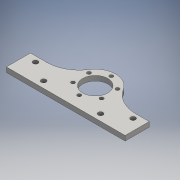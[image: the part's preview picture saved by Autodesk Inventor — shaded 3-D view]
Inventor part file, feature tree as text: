
AUTODESK INVENTOR PART (.ipt)
format: ipt  version: 2016 (Build 200138000, 138)  size: 146,432 bytes
history: native  units: mm
features: reference x13, extrude x4, sketch x4, fillet x1
ambient origin geometry x8: Origin, YZ Plane, XZ Plane, XY Plane, X Axis, Y Axis, Z Axis, Center Point
bodies: Solid1 (feature_tree)
feature tree (22):
  extrude  "Extrusion1"  Depth=6.0mm TaperAngle=0.0deg
  extrude  "Extrusion2"  Depth=6.0mm
  extrude  "Extrusion3"  Depth=60.0mm
  extrude  "Extrusion4"  Depth=40.0mm
  fillet  "Fillet2"  Radius=35.0mm
  sketch  "Sketch1"  dims[d0=34.0mm d1=6.0mm d2=0.0mm]
  reference  "Reference1"
  reference  "Reference2"
  reference  "Reference3"
  sketch  "Sketch2"  dims[d3=6.0mm d4=6.0mm]
  sketch  "Sketch3"  dims[d6=15.0mm d7=60.0mm]
  reference  "Reference5"
  reference  "Reference6"
  reference  "Reference7"
  reference  "Reference8"
  reference  "Reference9"
  reference  "Reference10"
  reference  "Reference11"
  sketch  "Sketch5"  dims[d8=6.0mm d9=0.0mm d10=8.0mm d11=35.0mm d12=6.0mm d13=0.0mm d14=0.5mm d16=6.0mm d17=0.0mm d18=40.0mm]
  reference  "Reference12"
  reference  "Reference13"
  reference  "Reference14"
